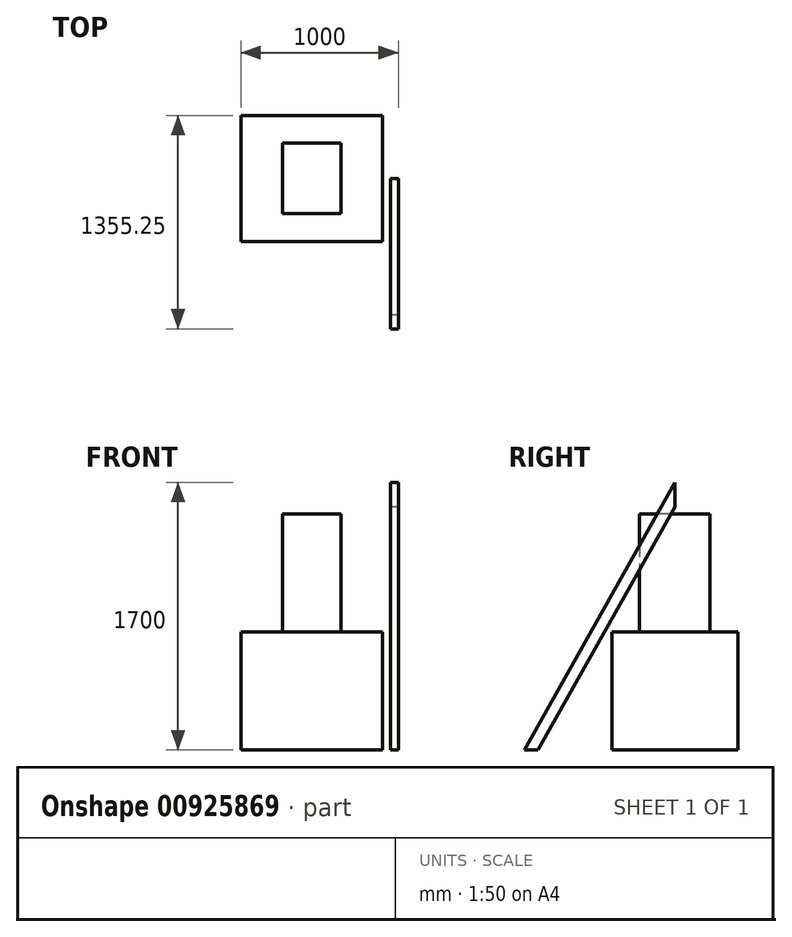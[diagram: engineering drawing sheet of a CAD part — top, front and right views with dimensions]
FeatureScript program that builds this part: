
annotation { "Feature Type Name" : "Feature", "Feature Type Description" : "" }
export const myFeature = defineFeature(function(context is Context, id is Id, definition is map)
    precondition{}
    {
        {
            var Q0;
            Q0=qCreatedBy(makeId("Top.planeOp"),FACE);
            var sketch = newSketch(context, id + "F0", { "sketchPlane" : qUnion([Q0])});
            skLineSegment(sketch, "E0.bottom", {"start": v(-450, 400) * mm, "end": v(450, 400) * mm});
            skLineSegment(sketch, "E0.top", {"start": v(-450, -400) * mm, "end": v(450, -400) * mm});
            skLineSegment(sketch, "E0.left", {"start": v(-450, 400) * mm, "end": v(-450, -400) * mm});
            skLineSegment(sketch, "E0.right", {"start": v(450, 400) * mm, "end": v(450, -400) * mm});
            skPoint(sketch, "E0.middle", {"position": v(0, 0) * mm});
            skSolve(sketch);
        }
        {
            var Q0;
            Q0 = qSketchRegion(id + "F0", true);
            extrude(context, id + "F1", {"entities" : qUnion([Q0]), "depth" : 750 * mm, "offsetDistance" : 25 * mm});
        }
        {
            var Q0;
            Q0=makeQuery(id+"F1.opExtrude","CAP_FACE",FACE,{"disambiguationData":[OSD([sQuery(id+"F0.wireOp",EDGE,"E0.bottom"),sQuery(id+"F0.wireOp",EDGE,"E0.top"),sQuery(id+"F0.wireOp",EDGE,"E0.left"),sQuery(id+"F0.wireOp",EDGE,"E0.right")])],"isStart":false});
            var sketch = newSketch(context, id + "F2", { "sketchPlane" : qUnion([Q0])});
            skLineSegment(sketch, "E1.bottom", {"start": v(-186.07, 224.3) * mm, "end": v(186.07, 224.3) * mm});
            skLineSegment(sketch, "E1.top", {"start": v(-186.07, -224.3) * mm, "end": v(186.07, -224.3) * mm});
            skLineSegment(sketch, "E1.left", {"start": v(-186.07, 224.3) * mm, "end": v(-186.07, -224.3) * mm});
            skLineSegment(sketch, "E1.right", {"start": v(186.07, 224.3) * mm, "end": v(186.07, -224.3) * mm});
            skPoint(sketch, "E1.middle", {"position": v(0, 0) * mm});
            skSolve(sketch);
        }
        {
            var Q0;
            Q0 = qSketchRegion(id + "F2", true);
            extrude(context, id + "F3", {"entities" : qUnion([Q0]), "operationType" : NewBodyOperationType.ADD, "depth" : 750 * mm, "offsetDistance" : 25 * mm});
        }
        {
            var Q0;
            Q0=qCreatedBy(makeId("Right.planeOp"),FACE);
            cPlane(context, id + "F4", {"entities" : qUnion([Q0]), "cplaneType" : CPlaneType.OFFSET, "offset" : 500 * mm, "width" : 150 * mm, "height" : 150 * mm});
        }
        {
            var Q0;
            Q0=qCreatedBy(id+"F4.planeOp",FACE);
            var sketch = newSketch(context, id + "F5", { "sketchPlane" : qUnion([Q0])});
            skLineSegment(sketch, "E2", {"start": v(0, 0) * mm, "end": v(0, 1874.15) * mm, "construction": true});
            skLineSegment(sketch, "E3", {"start": v(-955.25, 0) * mm, "end": v(0, 1700) * mm});
            skLineSegment(sketch, "E4.0", {"start": v(-868.07, 0) * mm, "end": v(0, 1544.86) * mm});
            skLineSegment(sketch, "E5", {"start": v(-955.25, 0) * mm, "end": v(-868.07, 0) * mm});
            skLineSegment(sketch, "E6", {"start": v(0, 1700) * mm, "end": v(0, 1544.86) * mm});
            skSolve(sketch);
        }
        {
            var Q0;
            Q0 = qSketchRegion(id + "F5", true);
            extrude(context, id + "F6", {"entities" : qUnion([Q0]), "depth" : 50 * mm, "offsetDistance" : 25 * mm});
        }
    });
